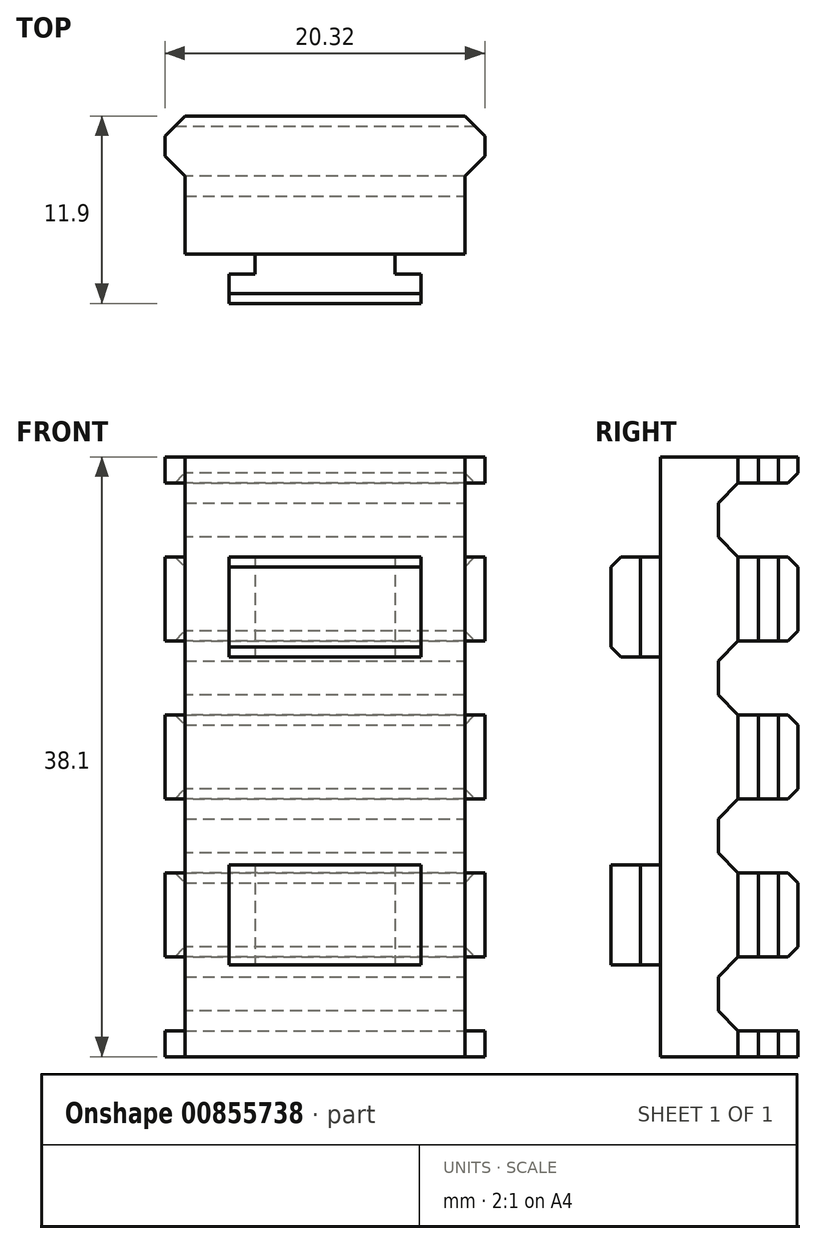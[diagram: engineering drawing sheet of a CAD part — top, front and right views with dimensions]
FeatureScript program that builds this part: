
annotation { "Feature Type Name" : "Feature", "Feature Type Description" : "" }
export const myFeature = defineFeature(function(context is Context, id is Id, definition is map)
    precondition{}
    {
        {
            var Q0;
            Q0=qCreatedBy(makeId("Top.planeOp"),FACE);
            var sketch = newSketch(context, id + "F0", { "sketchPlane" : qUnion([Q0])});
            skLineSegment(sketch, "E0.top", {"start": v(0, 4.95) * mm, "end": v(17.78, 4.95) * mm});
            skLineSegment(sketch, "E0.left", {"start": v(0, 0) * mm, "end": v(0, 4.95) * mm});
            skLineSegment(sketch, "E0.right", {"start": v(17.78, 0) * mm, "end": v(17.78, 4.95) * mm});
            skLineSegment(sketch, "E1", {"start": v(0, 4.95) * mm, "end": v(-1.27, 6.22) * mm});
            skLineSegment(sketch, "E2", {"start": v(-1.27, 6.22) * mm, "end": v(-1.27, 7.5) * mm});
            skLineSegment(sketch, "E3", {"start": v(-1.27, 7.5) * mm, "end": v(0, 8.76) * mm});
            skLineSegment(sketch, "E4", {"start": v(0, 8.76) * mm, "end": v(8.9, 8.76) * mm});
            skPoint(sketch, "E4.endSnap0", {"position": v(8.9, 4.95) * mm});
            skLineSegment(sketch, "E5", {"start": v(8.9, 4.95) * mm, "end": v(8.9, 13.15) * mm, "construction": true});
            skLineSegment(sketch, "E6.MirrorCS", {"start": v(17.78, 8.76) * mm, "end": v(8.9, 8.76) * mm});
            skLineSegment(sketch, "E7.MirrorCS", {"start": v(19.05, 7.5) * mm, "end": v(17.78, 8.76) * mm});
            skLineSegment(sketch, "E8.MirrorCS", {"start": v(19.05, 6.22) * mm, "end": v(19.05, 7.5) * mm});
            skLineSegment(sketch, "E9.MirrorCS", {"start": v(17.78, 4.95) * mm, "end": v(19.05, 6.22) * mm});
            skLineSegment(sketch, "E10", {"start": v(4.45, 0) * mm, "end": v(4.45, -1.27) * mm});
            skLineSegment(sketch, "E11", {"start": v(4.45, -1.27) * mm, "end": v(2.8, -1.27) * mm});
            skLineSegment(sketch, "E12", {"start": v(2.8, -1.27) * mm, "end": v(2.8, -3.14) * mm});
            skLineSegment(sketch, "E13", {"start": v(2.8, -3.14) * mm, "end": v(8.9, -3.14) * mm});
            skLineSegment(sketch, "E14.MirrorCS", {"start": v(14.99, -3.14) * mm, "end": v(8.9, -3.14) * mm});
            skLineSegment(sketch, "E15.MirrorCS", {"start": v(14.99, -1.27) * mm, "end": v(14.99, -3.14) * mm});
            skLineSegment(sketch, "E16.MirrorCS", {"start": v(13.33, -1.27) * mm, "end": v(14.99, -1.27) * mm});
            skLineSegment(sketch, "E17.MirrorCS", {"start": v(13.33, 0) * mm, "end": v(13.33, -1.27) * mm});
            skLineSegment(sketch, "E18", {"start": v(0, 0) * mm, "end": v(4.45, 0) * mm});
            skLineSegment(sketch, "E19", {"start": v(13.33, 0) * mm, "end": v(17.78, 0) * mm});
            skSolve(sketch);
        }
        {
            var Q0;
            Q0 = qSketchRegion(id + "F0", true);
            extrude(context, id + "F1", {"entities" : qUnion([Q0]), "depth" : 38.1 * mm, "offsetDistance" : 25.4 * mm});
        }
        {
            var Q0;
            Q0=makeQuery(id+"F1.opExtrude","SWEPT_FACE",FACE,{"disambiguationData":[OSD([sQuery(id+"F0.wireOp",EDGE,"E4"),sQuery(id+"F0.wireOp",EDGE,"E6.MirrorCS")])]});
            var sketch = newSketch(context, id + "F2", { "sketchPlane" : qUnion([Q0])});
            skLineSegment(sketch, "E20.bottom", {"start": v(1.27, 36.45) * mm, "end": v(-19.05, 36.45) * mm});
            skLineSegment(sketch, "E20.top", {"start": v(1.27, 31.75) * mm, "end": v(-19.05, 31.75) * mm});
            skLineSegment(sketch, "E20.left", {"start": v(1.27, 36.45) * mm, "end": v(1.27, 31.75) * mm});
            skLineSegment(sketch, "E20.right", {"start": v(-19.05, 36.45) * mm, "end": v(-19.05, 31.75) * mm});
            skLineSegment(sketch, "E21.bottom", {"start": v(1.27, 26.42) * mm, "end": v(-19.05, 26.42) * mm});
            skLineSegment(sketch, "E21.top", {"start": v(1.27, 21.72) * mm, "end": v(-19.05, 21.72) * mm});
            skLineSegment(sketch, "E21.left", {"start": v(1.27, 26.42) * mm, "end": v(1.27, 21.72) * mm});
            skLineSegment(sketch, "E21.right", {"start": v(-19.05, 26.42) * mm, "end": v(-19.05, 21.72) * mm});
            skLineSegment(sketch, "E22.bottom", {"start": v(1.27, 16.38) * mm, "end": v(-19.05, 16.38) * mm});
            skLineSegment(sketch, "E22.top", {"start": v(1.27, 11.68) * mm, "end": v(-19.05, 11.68) * mm});
            skLineSegment(sketch, "E22.left", {"start": v(1.27, 16.38) * mm, "end": v(1.27, 11.68) * mm});
            skLineSegment(sketch, "E22.right", {"start": v(-19.05, 16.38) * mm, "end": v(-19.05, 11.68) * mm});
            skLineSegment(sketch, "E23.bottom", {"start": v(1.27, 6.35) * mm, "end": v(-19.05, 6.35) * mm});
            skLineSegment(sketch, "E23.top", {"start": v(1.27, 1.65) * mm, "end": v(-19.05, 1.65) * mm});
            skLineSegment(sketch, "E23.left", {"start": v(1.27, 6.35) * mm, "end": v(1.27, 1.65) * mm});
            skLineSegment(sketch, "E23.right", {"start": v(-19.05, 6.35) * mm, "end": v(-19.05, 1.65) * mm});
            skSolve(sketch);
        }
        {
            var Q0;
            Q0 = qSketchRegion(id + "F2", true);
            extrude(context, id + "F3", {"entities" : qUnion([Q0]), "operationType" : NewBodyOperationType.REMOVE, "oppositeDirection" : true, "depth" : 5.08 * mm, "offsetDistance" : 25.4 * mm});
        }
        {
            var Q0;
            Q0=makeQuery(id+"F3.boolean.opBoolean","COPY",EDGE,{"derivedFrom":makeQuery(id+"F3.opExtrude","CAP_EDGE",EDGE,{"disambiguationData":[OSD([sQuery(id+"F2.wireOp",EDGE,"E20.bottom")])],"isStart":false})});
            var Q1;
            Q1=makeQuery(id+"F3.boolean.opBoolean","COPY",EDGE,{"derivedFrom":makeQuery(id+"F3.opExtrude","CAP_EDGE",EDGE,{"disambiguationData":[OSD([sQuery(id+"F2.wireOp",EDGE,"E20.top")])],"isStart":false})});
            var Q2;
            Q2=makeQuery(id+"F3.boolean.opBoolean","COPY",EDGE,{"derivedFrom":makeQuery(id+"F3.opExtrude","CAP_EDGE",EDGE,{"disambiguationData":[OSD([sQuery(id+"F2.wireOp",EDGE,"E21.bottom")])],"isStart":false})});
            var Q3;
            Q3=makeQuery(id+"F3.boolean.opBoolean","COPY",EDGE,{"derivedFrom":makeQuery(id+"F3.opExtrude","CAP_EDGE",EDGE,{"disambiguationData":[OSD([sQuery(id+"F2.wireOp",EDGE,"E21.top")])],"isStart":false})});
            var Q4;
            Q4=makeQuery(id+"F3.boolean.opBoolean","COPY",EDGE,{"derivedFrom":makeQuery(id+"F3.opExtrude","CAP_EDGE",EDGE,{"disambiguationData":[OSD([sQuery(id+"F2.wireOp",EDGE,"E22.bottom")])],"isStart":false})});
            var Q5;
            Q5=makeQuery(id+"F3.boolean.opBoolean","COPY",EDGE,{"derivedFrom":makeQuery(id+"F3.opExtrude","CAP_EDGE",EDGE,{"disambiguationData":[OSD([sQuery(id+"F2.wireOp",EDGE,"E22.top")])],"isStart":false})});
            var Q6;
            Q6=makeQuery(id+"F3.boolean.opBoolean","COPY",EDGE,{"derivedFrom":makeQuery(id+"F3.opExtrude","CAP_EDGE",EDGE,{"disambiguationData":[OSD([sQuery(id+"F2.wireOp",EDGE,"E23.bottom")])],"isStart":false})});
            var Q7;
            Q7=makeQuery(id+"F3.boolean.opBoolean","COPY",EDGE,{"derivedFrom":makeQuery(id+"F3.opExtrude","CAP_EDGE",EDGE,{"disambiguationData":[OSD([sQuery(id+"F2.wireOp",EDGE,"E23.top")])],"isStart":false})});
            chamfer(context, id + "F4", {"entities" : qUnion([Q0, Q1, Q2, Q3, Q4, Q5, Q6, Q7]), "width" : 1.27 * mm, "tangentPropagation" : true});
        }
        {
            var Q0;
            Q0=makeQuery(id+"F3.boolean.opBoolean","COPY",EDGE,{"derivedFrom":makeQuery(id+"F3.opExtrude","CAP_EDGE",EDGE,{"disambiguationData":[OSD([sQuery(id+"F2.wireOp",EDGE,"E20.top")])],"isStart":true})});
            var Q1;
            Q1=makeQuery(id+"F3.boolean.opBoolean","COPY",EDGE,{"derivedFrom":makeQuery(id+"F3.opExtrude","CAP_EDGE",EDGE,{"disambiguationData":[OSD([sQuery(id+"F2.wireOp",EDGE,"E21.bottom")])],"isStart":true})});
            var Q2;
            Q2=makeQuery(id+"F3.boolean.opBoolean","COPY",EDGE,{"derivedFrom":makeQuery(id+"F3.opExtrude","CAP_EDGE",EDGE,{"disambiguationData":[OSD([sQuery(id+"F2.wireOp",EDGE,"E21.top")])],"isStart":true})});
            var Q3;
            Q3=makeQuery(id+"F3.boolean.opBoolean","COPY",EDGE,{"derivedFrom":makeQuery(id+"F3.opExtrude","CAP_EDGE",EDGE,{"disambiguationData":[OSD([sQuery(id+"F2.wireOp",EDGE,"E22.bottom")])],"isStart":true})});
            var Q4;
            Q4=makeQuery(id+"F3.boolean.opBoolean","COPY",EDGE,{"derivedFrom":makeQuery(id+"F3.opExtrude","CAP_EDGE",EDGE,{"disambiguationData":[OSD([sQuery(id+"F2.wireOp",EDGE,"E22.top")])],"isStart":true})});
            var Q5;
            Q5=makeQuery(id+"F3.boolean.opBoolean","COPY",EDGE,{"derivedFrom":makeQuery(id+"F3.opExtrude","CAP_EDGE",EDGE,{"disambiguationData":[OSD([sQuery(id+"F2.wireOp",EDGE,"E23.bottom")])],"isStart":true})});
            var Q6;
            Q6=makeQuery(id+"F3.boolean.opBoolean","COPY",EDGE,{"derivedFrom":makeQuery(id+"F3.opExtrude","CAP_EDGE",EDGE,{"disambiguationData":[OSD([sQuery(id+"F2.wireOp",EDGE,"E23.top")])],"isStart":true})});
            var Q7;
            Q7=makeQuery(id+"F3.boolean.opBoolean","COPY",EDGE,{"derivedFrom":makeQuery(id+"F3.opExtrude","CAP_EDGE",EDGE,{"disambiguationData":[OSD([sQuery(id+"F2.wireOp",EDGE,"E20.bottom")])],"isStart":true})});
            chamfer(context, id + "F5", {"entities" : qUnion([Q0, Q1, Q2, Q3, Q4, Q5, Q6, Q7]), "width" : 0.64 * mm, "tangentPropagation" : true});
        }
        {
            var Q0;
            Q0=makeQuery(id+"F1.opExtrude","SWEPT_FACE",FACE,{"disambiguationData":[OSD([sQuery(id+"F0.wireOp",EDGE,"E0.right")])]});
            var sketch = newSketch(context, id + "F6", { "sketchPlane" : qUnion([Q0])});
            skLineSegment(sketch, "E24.bottom", {"start": v(0, 38.1) * mm, "end": v(-3.14, 38.1) * mm});
            skLineSegment(sketch, "E24.top", {"start": v(0, 31.75) * mm, "end": v(-3.14, 31.75) * mm});
            skLineSegment(sketch, "E24.left", {"start": v(0, 38.1) * mm, "end": v(0, 31.75) * mm});
            skLineSegment(sketch, "E24.right", {"start": v(-3.14, 38.1) * mm, "end": v(-3.14, 31.75) * mm});
            skLineSegment(sketch, "E25.bottom", {"start": v(0, 25.4) * mm, "end": v(-3.14, 25.4) * mm});
            skLineSegment(sketch, "E25.top", {"start": v(0, 12.2) * mm, "end": v(-3.14, 12.2) * mm});
            skLineSegment(sketch, "E25.left", {"start": v(0, 25.4) * mm, "end": v(0, 12.2) * mm});
            skLineSegment(sketch, "E25.right", {"start": v(-3.14, 25.4) * mm, "end": v(-3.14, 12.2) * mm});
            skLineSegment(sketch, "E26.bottom", {"start": v(0, 5.84) * mm, "end": v(-3.14, 5.84) * mm});
            skLineSegment(sketch, "E26.top", {"start": v(0, 0) * mm, "end": v(-3.14, 0) * mm});
            skLineSegment(sketch, "E26.left", {"start": v(0, 5.84) * mm, "end": v(0, 0) * mm});
            skLineSegment(sketch, "E26.right", {"start": v(-3.14, 5.84) * mm, "end": v(-3.14, 0) * mm});
            skSolve(sketch);
        }
        {
            var Q0;
            Q0 = qSketchRegion(id + "F6", true);
            extrude(context, id + "F7", {"entities" : qUnion([Q0]), "operationType" : NewBodyOperationType.REMOVE, "endBound" : BoundingType.THROUGH_ALL, "oppositeDirection" : true, "depth" : 25.4 * mm, "offsetDistance" : 25.4 * mm});
        }
        {
            var Q0;
            Q0=makeQuery(id+"F7.boolean.opBoolean","COPY",EDGE,{"derivedFrom":makeQuery(id+"F7.opExtrude","SWEPT_EDGE",EDGE,{"disambiguationData":[OSD([sQuery(id+"F6.wireOp",EDGE,"E24.top"),sQuery(id+"F6.wireOp",EDGE,"E24.right")])]})});
            var Q1;
            Q1=makeQuery(id+"F7.boolean.opBoolean","COPY",EDGE,{"derivedFrom":makeQuery(id+"F7.opExtrude","SWEPT_EDGE",EDGE,{"disambiguationData":[OSD([sQuery(id+"F6.wireOp",EDGE,"E25.top"),sQuery(id+"F6.wireOp",EDGE,"E25.right")])]})});
            var Q2;
            Q2=makeQuery(id+"F7.boolean.opBoolean","COPY",EDGE,{"derivedFrom":makeQuery(id+"F7.opExtrude","SWEPT_EDGE",EDGE,{"disambiguationData":[OSD([sQuery(id+"F6.wireOp",EDGE,"E25.bottom"),sQuery(id+"F6.wireOp",EDGE,"E25.right")])]})});
            var Q3;
            Q3=makeQuery(id+"F7.boolean.opBoolean","COPY",EDGE,{"derivedFrom":makeQuery(id+"F7.opExtrude","SWEPT_EDGE",EDGE,{"disambiguationData":[OSD([sQuery(id+"F6.wireOp",EDGE,"E26.bottom"),sQuery(id+"F6.wireOp",EDGE,"E26.right")])]})});
            chamfer(context, id + "F8", {"entities" : qUnion([Q0, Q1, Q2, Q3]), "width" : 0.64 * mm, "tangentPropagation" : true});
        }
    });
